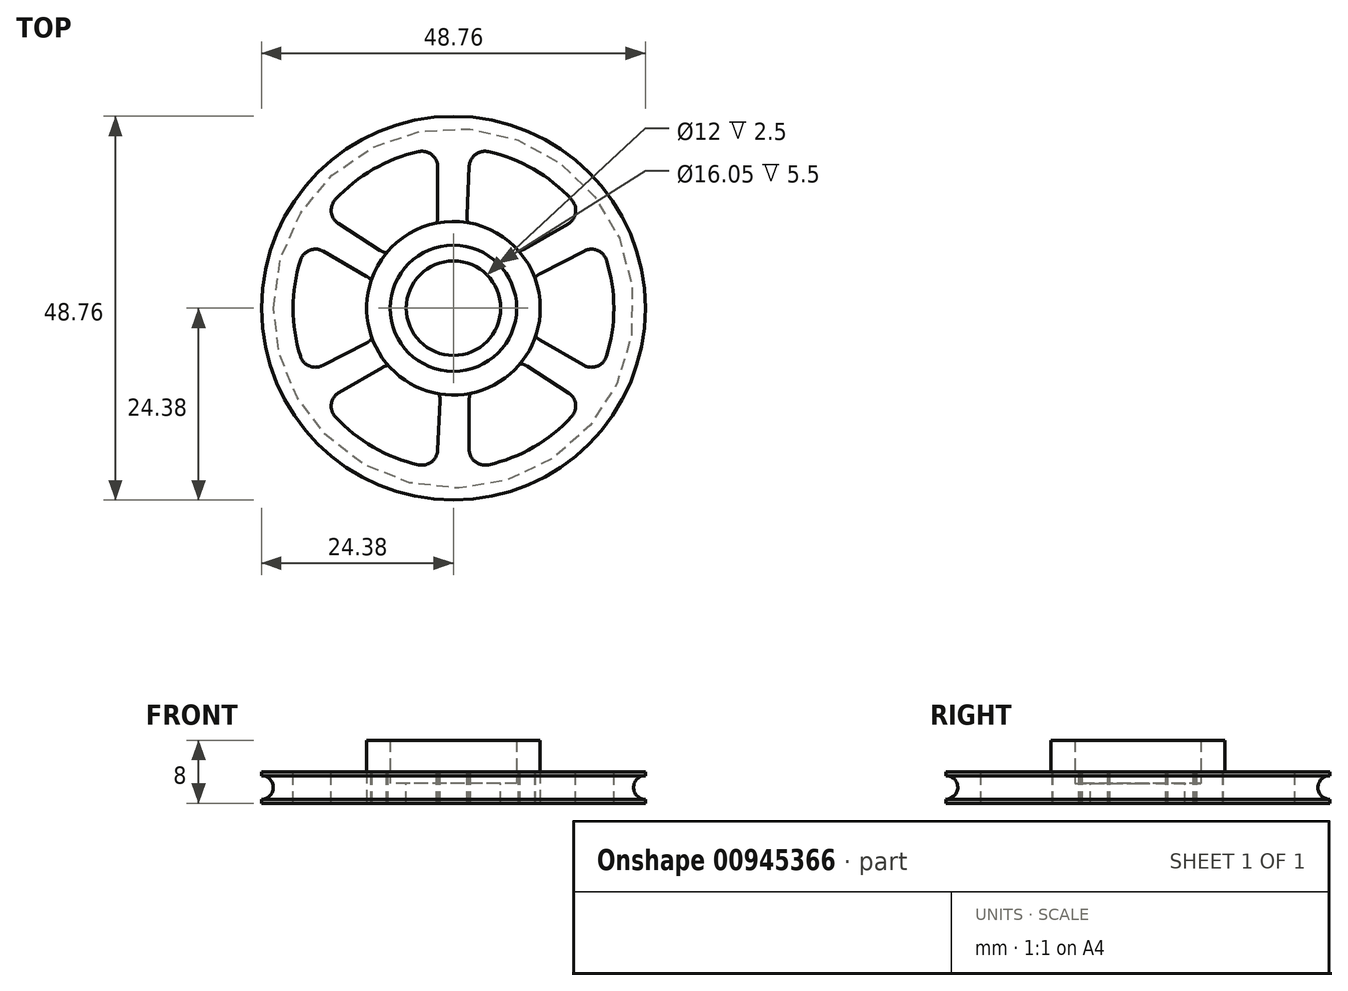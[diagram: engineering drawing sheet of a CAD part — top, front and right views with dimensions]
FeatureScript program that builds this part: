
annotation { "Feature Type Name" : "Feature", "Feature Type Description" : "" }
export const myFeature = defineFeature(function(context is Context, id is Id, definition is map)
    precondition{}
    {
        {
            var Q0;
            Q0=qCreatedBy(makeId("Top.planeOp"),FACE);
            var sketch = newSketch(context, id + "F0", { "sketchPlane" : qUnion([Q0])});
            skCircle(sketch, "E0", {"center": v(0, 0) * mm, "radius": 24.38 * mm});
            skSolve(sketch);
        }
        {
            var Q0;
            Q0=makeQuery(id+"F0.imprint","IMPRINT",FACE,{"disambiguationData":[TD([[makeQuery(id+"F0.imprint","IMPRINT",EDGE,{"derivedFrom":sQuery(id+"F0.wireOp",EDGE,"E0")}),1.0]])]});
            extrude(context, id + "F1", {"entities" : qUnion([Q0]), "depth" : 4 * mm, "offsetDistance" : 25.4 * mm});
        }
        {
            var Q0;
            Q0=makeQuery(id+"F1.opExtrude","CAP_FACE",FACE,{"disambiguationData":[OSD([sQuery(id+"F0.wireOp",EDGE,"E0"),sQuery(id+"F0.wireOp",EDGE,"n39IqKt5-bk1q-LU1x-fgod-8OyBNiFTd7FZ")])],"isStart":false});
            var sketch = newSketch(context, id + "F2", { "sketchPlane" : qUnion([Q0]), "disableImprinting" : false});
            skCircle(sketch, "E1", {"center": v(0, 0) * mm, "radius": 8.03 * mm});
            skCircle(sketch, "E2.0", {"center": v(0, 0) * mm, "radius": 11.03 * mm});
            skSolve(sketch);
        }
        {
            var Q0;
            Q0=qSketchRegion(id+"F2",true);
            extrude(context, id + "F3", {"entities" : qUnion([Q0]), "operationType" : NewBodyOperationType.ADD, "depth" : 4 * mm, "offsetDistance" : 25.4 * mm});
        }
        {
            var Q0;
            Q0=makeQuery(id+"F3.boolean.opBoolean","SPLIT",FACE,{"disambiguationData":[TD([makeQuery(id+"F3.opExtrude","SWEPT_FACE",FACE,{"disambiguationData":[OSD([sQuery(id+"F2.wireOp",EDGE,"E1")])]})])],"derivedFrom":makeQuery(id+"F1.opExtrude","CAP_FACE",FACE,{"disambiguationData":[OSD([sQuery(id+"F0.wireOp",EDGE,"E0")])],"isStart":false})});
            var sketch = newSketch(context, id + "F4", { "sketchPlane" : qUnion([Q0])});
            skCircle(sketch, "E3", {"center": v(0, 0) * mm, "radius": 6 * mm});
            skSolve(sketch);
        }
        {
            var Q0;
            Q0 = qSketchRegion(id + "F4", true);
            extrude(context, id + "F5", {"entities" : qUnion([Q0]), "operationType" : NewBodyOperationType.REMOVE, "flatOperationType" : FlatOperationType.REMOVE, "oppositeDirection" : true, "depth" : 9 * mm, "offsetDistance" : 25.4 * mm, "domain" : OperationDomain.MODEL});
        }
        {
            var Q0;
            Q0=qCreatedBy(makeId("Front.planeOp"),FACE);
            var sketch = newSketch(context, id + "F6", { "sketchPlane" : qUnion([Q0])});
            skCircle(sketch, "E4", {"center": v(-24.38, 2) * mm, "radius": 1.5 * mm});
            skLineSegment(sketch, "E5.bottom", {"start": v(-22.88, 0.65) * mm, "end": v(-25.02, 0.65) * mm});
            skLineSegment(sketch, "E5.top", {"start": v(-22.88, 3.35) * mm, "end": v(-25.02, 3.35) * mm});
            skLineSegment(sketch, "E5.left", {"start": v(-22.88, 0.65) * mm, "end": v(-22.88, 3.35) * mm});
            skLineSegment(sketch, "E5.right", {"start": v(-25.73, 1.35) * mm, "end": v(-25.73, 2.65) * mm});
            skLineSegment(sketch, "E6", {"start": v(0, 19.1) * mm, "end": v(0, -12.61) * mm, "construction": true});
            skLineSegment(sketch, "E7", {"start": v(-24.37, 3.35) * mm, "end": v(-22.88, 2) * mm});
            skLineSegment(sketch, "E8", {"start": v(-22.88, 2) * mm, "end": v(-24.38, 0.65) * mm});
            skLineSegment(sketch, "E9", {"start": v(-24.38, 0.65) * mm, "end": v(-24.37, 3.35) * mm});
            skSolve(sketch);
        }
        {
            var Q0;
            {var subQ0=sQuery(id+"F6.wireOp",EDGE,"E5.top");var subQ1=sQuery(id+"F6.wireOp",EDGE,"E4");var subQ2=makeQuery(id+"F6.imprint","INTERSECT",VERTEX,{"disambiguationData":[OD(0.0)],"derivedFrom":[subQ1,subQ0]});Q0=makeQuery(id+"F6.imprint","IMPRINT",FACE,{"disambiguationData":[TD([[makeQuery(id+"F6.imprint","IMPRINT",EDGE,{"disambiguationData":[TD([[subQ2,1.0]])],"derivedFrom":subQ1}),1.0]])]});}
            var Q1;
            {var subQ0=sQuery(id+"F6.wireOp",EDGE,"E5.bottom");var subQ1=sQuery(id+"F6.wireOp",EDGE,"E4");var subQ2=makeQuery(id+"F6.imprint","INTERSECT",VERTEX,{"disambiguationData":[OD(0.0)],"derivedFrom":[subQ1,subQ0]});Q1=makeQuery(id+"F6.imprint","IMPRINT",FACE,{"disambiguationData":[TD([[makeQuery(id+"F6.imprint","IMPRINT",EDGE,{"disambiguationData":[TD([[subQ2,-1.0]])],"derivedFrom":subQ1}),1.0]])]});}
            var Q2;
            {var subQ4=sQuery(id+"F6.wireOp",EDGE,"E5.right");Q2=makeQuery(id+"F6.imprint","IMPRINT",FACE,{"disambiguationData":[TD([[makeQuery(id+"F6.imprint","IMPRINT",EDGE,{"derivedFrom":subQ4}),-1.0]])]});}
            var Q3;
            {var subQ0=sQuery(id+"F6.wireOp",EDGE,"E7");Q3=makeQuery(id+"F6.imprint","IMPRINT",FACE,{"disambiguationData":[TD([[makeQuery(id+"F6.imprint","IMPRINT",EDGE,{"derivedFrom":subQ0}),1.0]])]});}
            var Q4;
            Q4=makeQuery(id+"F6.imprint","IMPRINT",FACE,{"disambiguationData":[TD([[makeQuery(id+"F6.imprint","IMPRINT",EDGE,{"derivedFrom":sQuery(id+"F6.wireOp",EDGE,"E7")}),-1.0]])]});
            var Q5;
            {var subQ0=sQuery(id+"F6.wireOp",EDGE,"E8");Q5=makeQuery(id+"F6.imprint","IMPRINT",FACE,{"disambiguationData":[TD([[makeQuery(id+"F6.imprint","IMPRINT",EDGE,{"derivedFrom":subQ0}),1.0]])]});}
            var Q6;
            Q6=sQuery(id+"F6.wireOp",EDGE,"E6");
            revolve(context, id + "F7", {"operationType" : NewBodyOperationType.REMOVE, "surfaceOperationType" : NewSurfaceOperationType.NEW, "entities" : qUnion([Q0, Q1, Q2, Q3, Q4, Q5]), "axis" : qUnion([Q6]), "revolveType" : RevolveType.FULL, "oppositeDirection" : true});
        }
        {
            var Q0;
            Q0=makeQuery(id+"F3.boolean.opBoolean","SPLIT",FACE,{"disambiguationData":[TD([makeQuery(id+"F3.opExtrude","SWEPT_FACE",FACE,{"disambiguationData":[OSD([sQuery(id+"F2.wireOp",EDGE,"E1")])]})])],"derivedFrom":makeQuery(id+"F1.opExtrude","CAP_FACE",FACE,{"disambiguationData":[OSD([sQuery(id+"F0.wireOp",EDGE,"E0")])],"isStart":false})});
            extrude(context, id + "F8", {"entities" : qUnion([Q0]), "operationType" : NewBodyOperationType.REMOVE, "flatOperationType" : FlatOperationType.REMOVE, "oppositeDirection" : true, "depth" : 1.5 * mm, "offsetDistance" : 25 * mm, "domain" : OperationDomain.MODEL});
        }
        {
            var Q0;
            Q0=makeQuery(id+"F2.imprint","IMPRINT",FACE,{"disambiguationData":[TD([[makeQuery(id+"F2.imprint","IMPRINT",EDGE,{"derivedFrom":sQuery(id+"F2.wireOp",EDGE,"E2.0")}),-1.0]])]});
            var sketch = newSketch(context, id + "F9", { "sketchPlane" : qUnion([Q0]), "disableImprinting" : false});
            skArc(sketch, "E10", {"start": v(-4.44, 19.89) * mm, "mid": v(-10.19, 17.65) * mm, "end": v(-15, 13.78) * mm});
            skArc(sketch, "E11", {"start": v(-3.35, 9.68) * mm, "mid": v(-5.24, 8.8) * mm, "end": v(-6.91, 7.56) * mm});
            skLineSegment(sketch, "E12.0", {"start": v(-2, 17.93) * mm, "end": v(-2, 11.57) * mm});
            skLineSegment(sketch, "E13.0", {"start": v(2, 18.03) * mm, "end": v(1.7, 11.77) * mm});
            skPoint(sketch, "E14.orphan", {"position": v(0, 21.24) * mm});
            skPoint(sketch, "E15.end.orphan", {"position": v(0, 11.01) * mm});
            skPoint(sketch, "E16.visualSharp", {"position": v(-2, 20.28) * mm});
            skArc(sketch, "E16.filletArc", {"start": v(-2, 17.93) * mm, "mid": v(-2.75, 19.5) * mm, "end": v(-4.44, 19.89) * mm});
            skPoint(sketch, "E17.visualSharp", {"position": v(2.11, 20.27) * mm});
            skArc(sketch, "E17.filletArc", {"start": v(4.44, 19.89) * mm, "mid": v(2.79, 19.52) * mm, "end": v(2, 18.03) * mm});
            skPoint(sketch, "E18.visualSharp", {"position": v(-2, 10.05) * mm});
            skArc(sketch, "E18.filletArc", {"start": v(-3.35, 9.68) * mm, "mid": v(-2.37, 10.41) * mm, "end": v(-2, 11.57) * mm});
            skPoint(sketch, "E19.visualSharp", {"position": v(1.62, 10.11) * mm});
            skArc(sketch, "E19.filletArc", {"start": v(1.7, 11.77) * mm, "mid": v(2.05, 10.53) * mm, "end": v(3.1, 9.77) * mm});
            skArc(sketch, "E20.1.0", {"start": v(-16.53, 7.24) * mm, "mid": v(-18.26, 7.37) * mm, "end": v(-19.44, 6.1) * mm});
            skArc(sketch, "E20.1.1", {"start": v(-15, 13.78) * mm, "mid": v(-15.52, 12.18) * mm, "end": v(-14.61, 10.75) * mm});
            skLineSegment(sketch, "E20.1.2", {"start": v(-14.61, 10.75) * mm, "end": v(-9.34, 7.36) * mm});
            skArc(sketch, "E20.1.3", {"start": v(-9.34, 7.36) * mm, "mid": v(-8.1, 7.04) * mm, "end": v(-6.91, 7.56) * mm});
            skArc(sketch, "E20.1.4", {"start": v(-10.06, 1.94) * mm, "mid": v(-10.2, 3.15) * mm, "end": v(-11.02, 4.05) * mm});
            skLineSegment(sketch, "E20.1.5", {"start": v(-16.53, 7.24) * mm, "end": v(-11.02, 4.05) * mm});
            skArc(sketch, "E20.2.0", {"start": v(-14.53, -10.7) * mm, "mid": v(-15.5, -12.13) * mm, "end": v(-15, -13.78) * mm});
            skArc(sketch, "E20.2.1", {"start": v(-19.44, -6.1) * mm, "mid": v(-18.3, -7.35) * mm, "end": v(-16.62, -7.28) * mm});
            skLineSegment(sketch, "E20.2.2", {"start": v(-16.62, -7.28) * mm, "end": v(-11.04, -4.41) * mm});
            skArc(sketch, "E20.2.3", {"start": v(-11.04, -4.41) * mm, "mid": v(-10.15, -3.49) * mm, "end": v(-10, -2.2) * mm});
            skArc(sketch, "E20.2.4", {"start": v(-6.71, -7.74) * mm, "mid": v(-7.83, -7.26) * mm, "end": v(-9.02, -7.52) * mm});
            skLineSegment(sketch, "E20.2.5", {"start": v(-14.53, -10.7) * mm, "end": v(-9.02, -7.52) * mm});
            skArc(sketch, "E20.3.0", {"start": v(2, -17.93) * mm, "mid": v(2.75, -19.5) * mm, "end": v(4.44, -19.89) * mm});
            skArc(sketch, "E20.3.1", {"start": v(-4.44, -19.89) * mm, "mid": v(-2.79, -19.52) * mm, "end": v(-2, -18.03) * mm});
            skLineSegment(sketch, "E20.3.2", {"start": v(-2, -18.03) * mm, "end": v(-1.7, -11.77) * mm});
            skArc(sketch, "E20.3.3", {"start": v(-1.7, -11.77) * mm, "mid": v(-2.05, -10.53) * mm, "end": v(-3.1, -9.77) * mm});
            skArc(sketch, "E20.3.4", {"start": v(3.35, -9.68) * mm, "mid": v(2.37, -10.41) * mm, "end": v(2, -11.57) * mm});
            skLineSegment(sketch, "E20.3.5", {"start": v(2, -17.93) * mm, "end": v(2, -11.57) * mm});
            skArc(sketch, "E20.4.0", {"start": v(16.53, -7.24) * mm, "mid": v(18.26, -7.37) * mm, "end": v(19.44, -6.1) * mm});
            skArc(sketch, "E20.4.1", {"start": v(15, -13.78) * mm, "mid": v(15.52, -12.18) * mm, "end": v(14.61, -10.75) * mm});
            skLineSegment(sketch, "E20.4.2", {"start": v(14.61, -10.75) * mm, "end": v(9.34, -7.36) * mm});
            skArc(sketch, "E20.4.3", {"start": v(9.34, -7.36) * mm, "mid": v(8.1, -7.04) * mm, "end": v(6.91, -7.56) * mm});
            skArc(sketch, "E20.4.4", {"start": v(10.06, -1.94) * mm, "mid": v(10.2, -3.15) * mm, "end": v(11.02, -4.05) * mm});
            skLineSegment(sketch, "E20.4.5", {"start": v(16.53, -7.24) * mm, "end": v(11.02, -4.05) * mm});
            skArc(sketch, "E20.5.0", {"start": v(14.53, 10.7) * mm, "mid": v(15.5, 12.13) * mm, "end": v(15, 13.78) * mm});
            skArc(sketch, "E20.5.1", {"start": v(19.44, 6.1) * mm, "mid": v(18.3, 7.35) * mm, "end": v(16.62, 7.28) * mm});
            skLineSegment(sketch, "E20.5.2", {"start": v(16.62, 7.28) * mm, "end": v(11.04, 4.41) * mm});
            skArc(sketch, "E20.5.3", {"start": v(11.04, 4.41) * mm, "mid": v(10.15, 3.49) * mm, "end": v(10, 2.2) * mm});
            skArc(sketch, "E20.5.4", {"start": v(6.71, 7.74) * mm, "mid": v(7.83, 7.26) * mm, "end": v(9.02, 7.52) * mm});
            skLineSegment(sketch, "E20.5.5", {"start": v(14.53, 10.7) * mm, "end": v(9.02, 7.52) * mm});
            skArc(sketch, "E21.trimOffspring", {"start": v(-19.44, 6.1) * mm, "mid": v(-20.38, 0) * mm, "end": v(-19.44, -6.1) * mm});
            skArc(sketch, "E22.trimOffspring", {"start": v(-10.06, 1.94) * mm, "mid": v(-10.24, -0.13) * mm, "end": v(-10, -2.2) * mm});
            skArc(sketch, "E23.trimOffspring", {"start": v(-6.71, -7.74) * mm, "mid": v(-5, -8.94) * mm, "end": v(-3.1, -9.77) * mm});
            skArc(sketch, "E24.trimOffspring", {"start": v(3.35, -9.68) * mm, "mid": v(5.24, -8.8) * mm, "end": v(6.91, -7.56) * mm});
            skArc(sketch, "E25.trimOffspring", {"start": v(10.06, -1.94) * mm, "mid": v(10.24, 0.13) * mm, "end": v(10, 2.2) * mm});
            skArc(sketch, "E26.trimOffspring", {"start": v(6.71, 7.74) * mm, "mid": v(5, 8.94) * mm, "end": v(3.1, 9.77) * mm});
            skArc(sketch, "E27.trimOffspring", {"start": v(15, 13.78) * mm, "mid": v(10.19, 17.65) * mm, "end": v(4.44, 19.89) * mm});
            skArc(sketch, "E28.trimOffspring", {"start": v(19.44, -6.1) * mm, "mid": v(20.38, 0) * mm, "end": v(19.44, 6.1) * mm});
            skArc(sketch, "E29.trimOffspring", {"start": v(4.44, -19.89) * mm, "mid": v(10.19, -17.65) * mm, "end": v(15, -13.78) * mm});
            skArc(sketch, "E30.trimOffspring", {"start": v(-15, -13.78) * mm, "mid": v(-10.19, -17.65) * mm, "end": v(-4.44, -19.89) * mm});
            skSolve(sketch);
        }
        {
            var Q0;
            Q0=makeQuery(id+"F9.imprint","IMPRINT",FACE,{"disambiguationData":[TD([[makeQuery(id+"F9.imprint","IMPRINT",EDGE,{"derivedFrom":sQuery(id+"F9.wireOp",EDGE,"E10")}),1.0]])]});
            var Q1;
            Q1=makeQuery(id+"F9.imprint","IMPRINT",FACE,{"disambiguationData":[TD([[makeQuery(id+"F9.imprint","IMPRINT",EDGE,{"derivedFrom":sQuery(id+"F9.wireOp",EDGE,"E13.0")}),1.0]])]});
            var Q2;
            Q2=makeQuery(id+"F9.imprint","IMPRINT",FACE,{"disambiguationData":[TD([[makeQuery(id+"F9.imprint","IMPRINT",EDGE,{"derivedFrom":sQuery(id+"F9.wireOp",EDGE,"E20.4.0")}),1.0]])]});
            var Q3;
            Q3=makeQuery(id+"F9.imprint","IMPRINT",FACE,{"disambiguationData":[TD([[makeQuery(id+"F9.imprint","IMPRINT",EDGE,{"derivedFrom":sQuery(id+"F9.wireOp",EDGE,"E20.3.0")}),1.0]])]});
            var Q4;
            Q4=makeQuery(id+"F9.imprint","IMPRINT",FACE,{"disambiguationData":[TD([[makeQuery(id+"F9.imprint","IMPRINT",EDGE,{"derivedFrom":sQuery(id+"F9.wireOp",EDGE,"E20.2.0")}),1.0]])]});
            var Q5;
            Q5=makeQuery(id+"F9.imprint","IMPRINT",FACE,{"disambiguationData":[TD([[makeQuery(id+"F9.imprint","IMPRINT",EDGE,{"derivedFrom":sQuery(id+"F9.wireOp",EDGE,"E20.1.0")}),1.0]])]});
            extrude(context, id + "F10", {"entities" : qUnion([Q0, Q1, Q2, Q3, Q4, Q5]), "operationType" : NewBodyOperationType.REMOVE, "oppositeDirection" : true, "depth" : 25 * mm, "offsetDistance" : 25 * mm});
        }
    });
